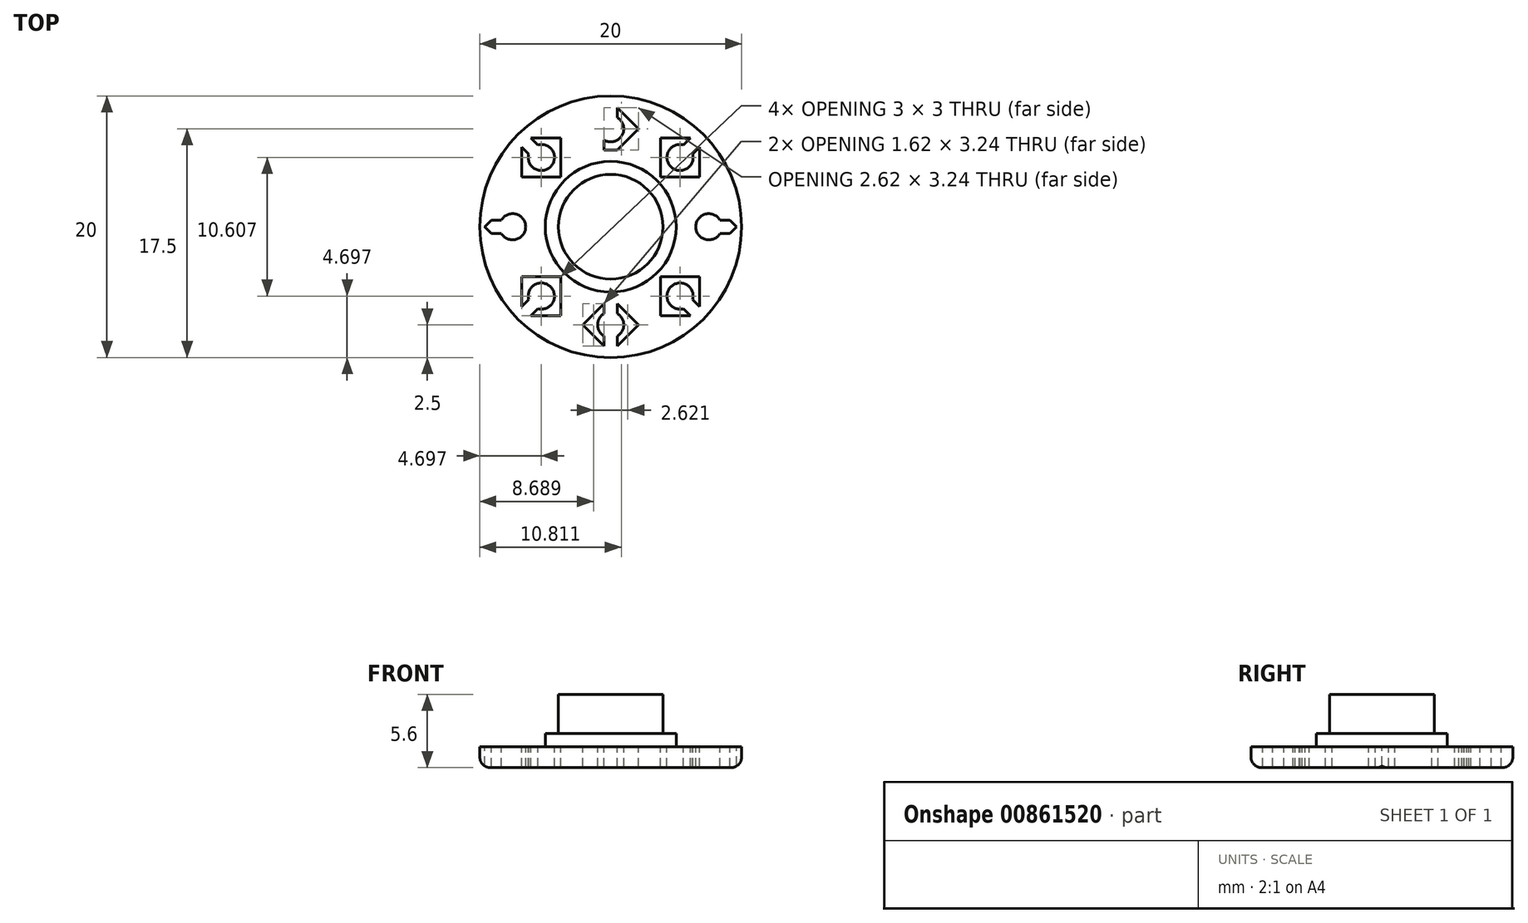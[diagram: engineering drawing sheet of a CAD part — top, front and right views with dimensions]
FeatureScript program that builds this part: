
annotation { "Feature Type Name" : "Feature", "Feature Type Description" : "" }
export const myFeature = defineFeature(function(context is Context, id is Id, definition is map)
    precondition{}
    {
        {
            var Q0;
            Q0=qCreatedBy(makeId("Top.planeOp"),FACE);
            var sketch = newSketch(context, id + "F0", { "sketchPlane" : qUnion([Q0])});
            skCircle(sketch, "E0", {"center": v(0, 0) * mm, "radius": 10 * mm});
            skSolve(sketch);
        }
        {
            var Q0;
            Q0=makeQuery(id+"F0.imprint","IMPRINT",FACE,{"disambiguationData":[TD([[makeQuery(id+"F0.imprint","IMPRINT",EDGE,{"derivedFrom":sQuery(id+"F0.wireOp",EDGE,"E0")}),1.0]])]});
            extrude(context, id + "F1", {"entities" : qUnion([Q0]), "depth" : 1.6 * mm, "offsetDistance" : 25 * mm});
        }
        {
            var Q0;
            Q0=makeQuery(id+"F1.opExtrude","CAP_FACE",FACE,{"disambiguationData":[OSD([sQuery(id+"F0.wireOp",EDGE,"E0")])],"isStart":false});
            var sketch = newSketch(context, id + "F2", { "sketchPlane" : qUnion([Q0])});
            skCircle(sketch, "E1", {"center": v(0, 0) * mm, "radius": 5 * mm});
            skSolve(sketch);
        }
        {
            var Q0;
            Q0=makeQuery(id+"F2.imprint","IMPRINT",FACE,{"disambiguationData":[TD([[makeQuery(id+"F2.imprint","IMPRINT",EDGE,{"derivedFrom":sQuery(id+"F2.wireOp",EDGE,"E1")}),1.0]])]});
            extrude(context, id + "F3", {"entities" : qUnion([Q0]), "operationType" : NewBodyOperationType.ADD, "depth" : 1 * mm, "offsetDistance" : 25 * mm});
        }
        {
            var Q0;
            Q0=makeQuery(id+"F3.opExtrude","CAP_FACE",FACE,{"disambiguationData":[OSD([sQuery(id+"F2.wireOp",EDGE,"E1")])],"isStart":false});
            var sketch = newSketch(context, id + "F4", { "sketchPlane" : qUnion([Q0])});
            skCircle(sketch, "E2", {"center": v(0, 0) * mm, "radius": 4 * mm});
            skSolve(sketch);
        }
        {
            var Q0;
            Q0=makeQuery(id+"F4.imprint","IMPRINT",FACE,{"disambiguationData":[TD([[makeQuery(id+"F4.imprint","IMPRINT",EDGE,{"derivedFrom":sQuery(id+"F4.wireOp",EDGE,"E2")}),1.0]])]});
            extrude(context, id + "F5", {"entities" : qUnion([Q0]), "depth" : 3 * mm, "offsetDistance" : 25 * mm});
        }
        {
            var Q0;
            Q0=makeQuery(id+"F1.opExtrude","CAP_FACE",FACE,{"disambiguationData":[OSD([sQuery(id+"F0.wireOp",EDGE,"E0")])],"isStart":false});
            var sketch = newSketch(context, id + "F6", { "sketchPlane" : qUnion([Q0])});
            skLineSegment(sketch, "E3", {"start": v(0, 5.38) * mm, "end": v(-2.12, 7.5) * mm});
            skLineSegment(sketch, "E4", {"start": v(-2.12, 7.5) * mm, "end": v(0, 9.62) * mm});
            skLineSegment(sketch, "E5", {"start": v(0, 5.38) * mm, "end": v(2.12, 7.5) * mm});
            skLineSegment(sketch, "E6", {"start": v(2.12, 7.5) * mm, "end": v(0, 9.62) * mm});
            skLineSegment(sketch, "E7", {"start": v(0, 5.38) * mm, "end": v(0, 5) * mm});
            skLineSegment(sketch, "E8", {"start": v(0, 9.62) * mm, "end": v(0, 10) * mm});
            skCircle(sketch, "E9", {"center": v(0, 7.5) * mm, "radius": 1 * mm});
            skCircle(sketch, "E10", {"center": v(0, 7.5) * mm, "radius": 2.12 * mm});
            skLineSegment(sketch, "E11", {"start": v(-0.5, 9.12) * mm, "end": v(0.5, 9.12) * mm});
            skLineSegment(sketch, "E12", {"start": v(0.5, 9.12) * mm, "end": v(0.5, 5.88) * mm});
            skLineSegment(sketch, "E13", {"start": v(0.5, 5.88) * mm, "end": v(-0.5, 5.88) * mm});
            skLineSegment(sketch, "E14", {"start": v(-0.5, 5.88) * mm, "end": v(-0.5, 9.12) * mm});
            skLineSegment(sketch, "E15.1.0", {"start": v(-6.8, 3.8) * mm, "end": v(-6.8, 6.8) * mm});
            skLineSegment(sketch, "E15.1.1", {"start": v(-3.8, 6.8) * mm, "end": v(-6.8, 6.8) * mm});
            skLineSegment(sketch, "E15.1.2", {"start": v(-3.8, 3.8) * mm, "end": v(-3.8, 6.8) * mm});
            skLineSegment(sketch, "E15.1.3", {"start": v(-3.8, 3.8) * mm, "end": v(-6.8, 3.8) * mm});
            skLineSegment(sketch, "E15.1.4", {"start": v(-4.51, 3.8) * mm, "end": v(-6.8, 6.1) * mm});
            skLineSegment(sketch, "E15.1.5", {"start": v(-6.1, 6.8) * mm, "end": v(-3.8, 4.51) * mm});
            skCircle(sketch, "E15.1.6", {"center": v(-5.3, 5.3) * mm, "radius": 1 * mm});
            skLineSegment(sketch, "E15.2.0", {"start": v(-7.5, -2.12) * mm, "end": v(-9.62, 0) * mm});
            skLineSegment(sketch, "E15.2.1", {"start": v(-7.5, 2.12) * mm, "end": v(-9.62, 0) * mm});
            skLineSegment(sketch, "E15.2.2", {"start": v(-5.38, 0) * mm, "end": v(-7.5, 2.12) * mm});
            skLineSegment(sketch, "E15.2.3", {"start": v(-5.38, 0) * mm, "end": v(-7.5, -2.12) * mm});
            skLineSegment(sketch, "E15.2.4", {"start": v(-5.88, -0.5) * mm, "end": v(-9.12, -0.5) * mm});
            skLineSegment(sketch, "E15.2.5", {"start": v(-9.12, 0.5) * mm, "end": v(-5.88, 0.5) * mm});
            skCircle(sketch, "E15.2.6", {"center": v(-7.5, 0) * mm, "radius": 1 * mm});
            skLineSegment(sketch, "E15.3.0", {"start": v(-3.8, -6.8) * mm, "end": v(-6.8, -6.8) * mm});
            skLineSegment(sketch, "E15.3.1", {"start": v(-6.8, -3.8) * mm, "end": v(-6.8, -6.8) * mm});
            skLineSegment(sketch, "E15.3.2", {"start": v(-3.8, -3.8) * mm, "end": v(-6.8, -3.8) * mm});
            skLineSegment(sketch, "E15.3.3", {"start": v(-3.8, -3.8) * mm, "end": v(-3.8, -6.8) * mm});
            skLineSegment(sketch, "E15.3.4", {"start": v(-3.8, -4.51) * mm, "end": v(-6.1, -6.8) * mm});
            skLineSegment(sketch, "E15.3.5", {"start": v(-6.8, -6.1) * mm, "end": v(-4.51, -3.8) * mm});
            skCircle(sketch, "E15.3.6", {"center": v(-5.3, -5.3) * mm, "radius": 1 * mm});
            skLineSegment(sketch, "E15.4.0", {"start": v(2.12, -7.5) * mm, "end": v(0, -9.62) * mm});
            skLineSegment(sketch, "E15.4.1", {"start": v(-2.12, -7.5) * mm, "end": v(0, -9.62) * mm});
            skLineSegment(sketch, "E15.4.2", {"start": v(0, -5.38) * mm, "end": v(-2.12, -7.5) * mm});
            skLineSegment(sketch, "E15.4.3", {"start": v(0, -5.38) * mm, "end": v(2.12, -7.5) * mm});
            skLineSegment(sketch, "E15.4.4", {"start": v(0.5, -5.88) * mm, "end": v(0.5, -9.12) * mm});
            skLineSegment(sketch, "E15.4.5", {"start": v(-0.5, -9.12) * mm, "end": v(-0.5, -5.88) * mm});
            skCircle(sketch, "E15.4.6", {"center": v(0, -7.5) * mm, "radius": 1 * mm});
            skLineSegment(sketch, "E15.5.0", {"start": v(6.8, -3.8) * mm, "end": v(6.8, -6.8) * mm});
            skLineSegment(sketch, "E15.5.1", {"start": v(3.8, -6.8) * mm, "end": v(6.8, -6.8) * mm});
            skLineSegment(sketch, "E15.5.2", {"start": v(3.8, -3.8) * mm, "end": v(3.8, -6.8) * mm});
            skLineSegment(sketch, "E15.5.3", {"start": v(3.8, -3.8) * mm, "end": v(6.8, -3.8) * mm});
            skLineSegment(sketch, "E15.5.4", {"start": v(4.51, -3.8) * mm, "end": v(6.8, -6.1) * mm});
            skLineSegment(sketch, "E15.5.5", {"start": v(6.1, -6.8) * mm, "end": v(3.8, -4.51) * mm});
            skCircle(sketch, "E15.5.6", {"center": v(5.3, -5.3) * mm, "radius": 1 * mm});
            skLineSegment(sketch, "E15.6.0", {"start": v(7.5, 2.12) * mm, "end": v(9.62, 0) * mm});
            skLineSegment(sketch, "E15.6.1", {"start": v(7.5, -2.12) * mm, "end": v(9.62, 0) * mm});
            skLineSegment(sketch, "E15.6.2", {"start": v(5.38, 0) * mm, "end": v(7.5, -2.12) * mm});
            skLineSegment(sketch, "E15.6.3", {"start": v(5.38, 0) * mm, "end": v(7.5, 2.12) * mm});
            skLineSegment(sketch, "E15.6.4", {"start": v(5.88, 0.5) * mm, "end": v(9.12, 0.5) * mm});
            skLineSegment(sketch, "E15.6.5", {"start": v(9.12, -0.5) * mm, "end": v(5.88, -0.5) * mm});
            skCircle(sketch, "E15.6.6", {"center": v(7.5, 0) * mm, "radius": 1 * mm});
            skLineSegment(sketch, "E15.7.0", {"start": v(3.8, 6.8) * mm, "end": v(6.8, 6.8) * mm});
            skLineSegment(sketch, "E15.7.1", {"start": v(6.8, 3.8) * mm, "end": v(6.8, 6.8) * mm});
            skLineSegment(sketch, "E15.7.2", {"start": v(3.8, 3.8) * mm, "end": v(6.8, 3.8) * mm});
            skLineSegment(sketch, "E15.7.3", {"start": v(3.8, 3.8) * mm, "end": v(3.8, 6.8) * mm});
            skLineSegment(sketch, "E15.7.4", {"start": v(3.8, 4.51) * mm, "end": v(6.1, 6.8) * mm});
            skLineSegment(sketch, "E15.7.5", {"start": v(6.8, 6.1) * mm, "end": v(4.51, 3.8) * mm});
            skCircle(sketch, "E15.7.6", {"center": v(5.3, 5.3) * mm, "radius": 1 * mm});
            skPoint(sketch, "E15.center", {"position": v(0, 0) * mm});
            skSolve(sketch);
        }
        {
            var Q0;
            Q0=makeQuery(id+"F1.opExtrude","CAP_EDGE",EDGE,{"disambiguationData":[OSD([sQuery(id+"F0.wireOp",EDGE,"E0")])],"isStart":true});
            fillet(context, id + "F7", {"entities" : qUnion([Q0]), "radius" : .8 * mm, "tangentPropagation" : true, "allowEdgeOverflow" : false});
        }
        {
            var Q0;
            {var subQ0=sQuery(id+"F6.wireOp",EDGE,"E14");var subQ3=sQuery(id+"F6.wireOp",EDGE,"E9");var subQ5=makeQuery(id+"F6.imprint","INTERSECT",VERTEX,{"disambiguationData":[OD(0.0)],"derivedFrom":[subQ3,subQ0]});Q0=makeQuery(id+"F6.imprint","IMPRINT",FACE,{"disambiguationData":[TD([[makeQuery(id+"F6.imprint","IMPRINT",EDGE,{"disambiguationData":[TD([[subQ5,-1.0]])],"derivedFrom":subQ3}),-1.0]])]});}
            var Q1;
            {var subQ0=sQuery(id+"F6.wireOp",EDGE,"E12");var subQ1=sQuery(id+"F6.wireOp",EDGE,"E9");var subQ2=makeQuery(id+"F6.imprint","INTERSECT",VERTEX,{"disambiguationData":[OD(0.0)],"derivedFrom":[subQ1,subQ0]});Q1=makeQuery(id+"F6.imprint","IMPRINT",FACE,{"disambiguationData":[TD([[makeQuery(id+"F6.imprint","IMPRINT",EDGE,{"disambiguationData":[TD([[subQ2,1.0]])],"derivedFrom":subQ1}),-1.0]])]});}
            var Q2;
            {var subQ1=sQuery(id+"F6.wireOp",EDGE,"E15.7.3");var subQ5=sQuery(id+"F6.wireOp",EDGE,"E15.7.0");var subQ6=makeQuery(id+"F6.imprint","INTERSECT",VERTEX,{"derivedFrom":[subQ5,subQ1]});Q2=makeQuery(id+"F6.imprint","IMPRINT",FACE,{"disambiguationData":[TD([[makeQuery(id+"F6.imprint","IMPRINT",EDGE,{"disambiguationData":[TD([[subQ6,-1.0]])],"derivedFrom":subQ5}),-1.0]])]});}
            var Q3;
            {var subQ1=sQuery(id+"F6.wireOp",EDGE,"E15.7.2");var subQ5=sQuery(id+"F6.wireOp",EDGE,"E15.7.1");var subQ6=makeQuery(id+"F6.imprint","INTERSECT",VERTEX,{"derivedFrom":[subQ5,subQ1]});Q3=makeQuery(id+"F6.imprint","IMPRINT",FACE,{"disambiguationData":[TD([[makeQuery(id+"F6.imprint","IMPRINT",EDGE,{"disambiguationData":[TD([[subQ6,-1.0]])],"derivedFrom":subQ5}),1.0]])]});}
            var Q4;
            {var subQ0=sQuery(id+"F6.wireOp",EDGE,"E15.6.6");var subQ1=sQuery(id+"F6.wireOp",EDGE,"E15.6.4");var subQ2=makeQuery(id+"F6.imprint","INTERSECT",VERTEX,{"disambiguationData":[OD(0.0)],"derivedFrom":[subQ1,subQ0]});Q4=makeQuery(id+"F6.imprint","IMPRINT",FACE,{"disambiguationData":[TD([[makeQuery(id+"F6.imprint","IMPRINT",EDGE,{"disambiguationData":[TD([[subQ2,-1.0]])],"derivedFrom":subQ1}),-1.0]])]});}
            var Q5;
            {var subQ1=sQuery(id+"F6.wireOp",EDGE,"E15.6.0");var subQ5=sQuery(id+"F6.wireOp",EDGE,"E15.6.1");var subQ6=makeQuery(id+"F6.imprint","INTERSECT",VERTEX,{"derivedFrom":[subQ1,subQ5]});Q5=makeQuery(id+"F6.imprint","IMPRINT",FACE,{"disambiguationData":[TD([[makeQuery(id+"F6.imprint","IMPRINT",EDGE,{"disambiguationData":[TD([[subQ6,1.0]])],"derivedFrom":subQ1}),-1.0]])]});}
            var Q6;
            {var subQ0=sQuery(id+"F6.wireOp",EDGE,"E15.6.6");var subQ1=sQuery(id+"F6.wireOp",EDGE,"E15.6.4");var subQ2=makeQuery(id+"F6.imprint","INTERSECT",VERTEX,{"disambiguationData":[OD(0.0)],"derivedFrom":[subQ1,subQ0]});Q6=makeQuery(id+"F6.imprint","IMPRINT",FACE,{"disambiguationData":[TD([[makeQuery(id+"F6.imprint","IMPRINT",EDGE,{"disambiguationData":[TD([[subQ2,-1.0]])],"derivedFrom":subQ1}),1.0]])]});}
            var Q7;
            {var subQ0=sQuery(id+"F6.wireOp",EDGE,"E15.6.6");var subQ1=sQuery(id+"F6.wireOp",EDGE,"E15.6.5");var subQ2=makeQuery(id+"F6.imprint","INTERSECT",VERTEX,{"disambiguationData":[OD(0.0)],"derivedFrom":[subQ1,subQ0]});Q7=makeQuery(id+"F6.imprint","IMPRINT",FACE,{"disambiguationData":[TD([[makeQuery(id+"F6.imprint","IMPRINT",EDGE,{"disambiguationData":[TD([[subQ2,-1.0]])],"derivedFrom":subQ1}),1.0]])]});}
            var Q8;
            {var subQ1=sQuery(id+"F6.wireOp",EDGE,"E15.2.0");var subQ5=sQuery(id+"F6.wireOp",EDGE,"E15.2.1");var subQ6=makeQuery(id+"F6.imprint","INTERSECT",VERTEX,{"derivedFrom":[subQ1,subQ5]});Q8=makeQuery(id+"F6.imprint","IMPRINT",FACE,{"disambiguationData":[TD([[makeQuery(id+"F6.imprint","IMPRINT",EDGE,{"disambiguationData":[TD([[subQ6,1.0]])],"derivedFrom":subQ1}),-1.0]])]});}
            var Q9;
            {var subQ0=sQuery(id+"F6.wireOp",EDGE,"E15.2.6");var subQ1=sQuery(id+"F6.wireOp",EDGE,"E15.2.5");var subQ2=makeQuery(id+"F6.imprint","INTERSECT",VERTEX,{"disambiguationData":[OD(0.0)],"derivedFrom":[subQ1,subQ0]});Q9=makeQuery(id+"F6.imprint","IMPRINT",FACE,{"disambiguationData":[TD([[makeQuery(id+"F6.imprint","IMPRINT",EDGE,{"disambiguationData":[TD([[subQ2,-1.0]])],"derivedFrom":subQ1}),1.0]])]});}
            var Q10;
            {var subQ0=sQuery(id+"F6.wireOp",EDGE,"E15.2.6");var subQ1=sQuery(id+"F6.wireOp",EDGE,"E15.2.4");var subQ2=makeQuery(id+"F6.imprint","INTERSECT",VERTEX,{"disambiguationData":[OD(0.0)],"derivedFrom":[subQ1,subQ0]});Q10=makeQuery(id+"F6.imprint","IMPRINT",FACE,{"disambiguationData":[TD([[makeQuery(id+"F6.imprint","IMPRINT",EDGE,{"disambiguationData":[TD([[subQ2,-1.0]])],"derivedFrom":subQ1}),-1.0]])]});}
            var Q11;
            {var subQ0=sQuery(id+"F6.wireOp",EDGE,"E15.2.6");var subQ1=sQuery(id+"F6.wireOp",EDGE,"E15.2.4");var subQ2=makeQuery(id+"F6.imprint","INTERSECT",VERTEX,{"disambiguationData":[OD(0.0)],"derivedFrom":[subQ1,subQ0]});Q11=makeQuery(id+"F6.imprint","IMPRINT",FACE,{"disambiguationData":[TD([[makeQuery(id+"F6.imprint","IMPRINT",EDGE,{"disambiguationData":[TD([[subQ2,-1.0]])],"derivedFrom":subQ1}),1.0]])]});}
            var Q12;
            {var subQ1=sQuery(id+"F6.wireOp",EDGE,"E15.4.2");var subQ5=sQuery(id+"F6.wireOp",EDGE,"E15.4.1");var subQ6=makeQuery(id+"F6.imprint","INTERSECT",VERTEX,{"derivedFrom":[subQ5,subQ1]});Q12=makeQuery(id+"F6.imprint","IMPRINT",FACE,{"disambiguationData":[TD([[makeQuery(id+"F6.imprint","IMPRINT",EDGE,{"disambiguationData":[TD([[subQ6,-1.0]])],"derivedFrom":subQ5}),1.0]])]});}
            var Q13;
            {var subQ1=sQuery(id+"F6.wireOp",EDGE,"E15.4.3");var subQ5=sQuery(id+"F6.wireOp",EDGE,"E15.4.0");var subQ6=makeQuery(id+"F6.imprint","INTERSECT",VERTEX,{"derivedFrom":[subQ5,subQ1]});Q13=makeQuery(id+"F6.imprint","IMPRINT",FACE,{"disambiguationData":[TD([[makeQuery(id+"F6.imprint","IMPRINT",EDGE,{"disambiguationData":[TD([[subQ6,-1.0]])],"derivedFrom":subQ5}),-1.0]])]});}
            var Q14;
            {var subQ1=sQuery(id+"F6.wireOp",EDGE,"E15.5.3");var subQ5=sQuery(id+"F6.wireOp",EDGE,"E15.5.0");var subQ6=makeQuery(id+"F6.imprint","INTERSECT",VERTEX,{"derivedFrom":[subQ5,subQ1]});Q14=makeQuery(id+"F6.imprint","IMPRINT",FACE,{"disambiguationData":[TD([[makeQuery(id+"F6.imprint","IMPRINT",EDGE,{"disambiguationData":[TD([[subQ6,-1.0]])],"derivedFrom":subQ5}),-1.0]])]});}
            var Q15;
            {var subQ1=sQuery(id+"F6.wireOp",EDGE,"E15.5.2");var subQ6=sQuery(id+"F6.wireOp",EDGE,"E15.5.3");var subQ9=makeQuery(id+"F6.imprint","INTERSECT",VERTEX,{"derivedFrom":[subQ1,subQ6]});Q15=makeQuery(id+"F6.imprint","IMPRINT",FACE,{"disambiguationData":[TD([[makeQuery(id+"F6.imprint","IMPRINT",EDGE,{"disambiguationData":[TD([[subQ9,-1.0]])],"derivedFrom":subQ1}),1.0]])]});}
            var Q16;
            {var subQ1=sQuery(id+"F6.wireOp",EDGE,"E15.5.2");var subQ5=sQuery(id+"F6.wireOp",EDGE,"E15.5.1");var subQ6=makeQuery(id+"F6.imprint","INTERSECT",VERTEX,{"derivedFrom":[subQ5,subQ1]});Q16=makeQuery(id+"F6.imprint","IMPRINT",FACE,{"disambiguationData":[TD([[makeQuery(id+"F6.imprint","IMPRINT",EDGE,{"disambiguationData":[TD([[subQ6,-1.0]])],"derivedFrom":subQ5}),1.0]])]});}
            var Q17;
            {var subQ1=sQuery(id+"F6.wireOp",EDGE,"E15.3.2");var subQ5=sQuery(id+"F6.wireOp",EDGE,"E15.3.1");var subQ6=makeQuery(id+"F6.imprint","INTERSECT",VERTEX,{"derivedFrom":[subQ5,subQ1]});Q17=makeQuery(id+"F6.imprint","IMPRINT",FACE,{"disambiguationData":[TD([[makeQuery(id+"F6.imprint","IMPRINT",EDGE,{"disambiguationData":[TD([[subQ6,-1.0]])],"derivedFrom":subQ5}),1.0]])]});}
            var Q18;
            {var subQ1=sQuery(id+"F6.wireOp",EDGE,"E15.3.2");var subQ6=sQuery(id+"F6.wireOp",EDGE,"E15.3.3");var subQ9=makeQuery(id+"F6.imprint","INTERSECT",VERTEX,{"derivedFrom":[subQ1,subQ6]});Q18=makeQuery(id+"F6.imprint","IMPRINT",FACE,{"disambiguationData":[TD([[makeQuery(id+"F6.imprint","IMPRINT",EDGE,{"disambiguationData":[TD([[subQ9,-1.0]])],"derivedFrom":subQ1}),1.0]])]});}
            var Q19;
            {var subQ1=sQuery(id+"F6.wireOp",EDGE,"E15.3.3");var subQ5=sQuery(id+"F6.wireOp",EDGE,"E15.3.0");var subQ6=makeQuery(id+"F6.imprint","INTERSECT",VERTEX,{"derivedFrom":[subQ5,subQ1]});Q19=makeQuery(id+"F6.imprint","IMPRINT",FACE,{"disambiguationData":[TD([[makeQuery(id+"F6.imprint","IMPRINT",EDGE,{"disambiguationData":[TD([[subQ6,-1.0]])],"derivedFrom":subQ5}),-1.0]])]});}
            var Q20;
            {var subQ1=sQuery(id+"F6.wireOp",EDGE,"E15.7.2");var subQ6=sQuery(id+"F6.wireOp",EDGE,"E15.7.3");var subQ9=makeQuery(id+"F6.imprint","INTERSECT",VERTEX,{"derivedFrom":[subQ1,subQ6]});Q20=makeQuery(id+"F6.imprint","IMPRINT",FACE,{"disambiguationData":[TD([[makeQuery(id+"F6.imprint","IMPRINT",EDGE,{"disambiguationData":[TD([[subQ9,-1.0]])],"derivedFrom":subQ1}),1.0]])]});}
            var Q21;
            {var subQ1=sQuery(id+"F6.wireOp",EDGE,"E15.1.3");var subQ5=sQuery(id+"F6.wireOp",EDGE,"E15.1.0");var subQ6=makeQuery(id+"F6.imprint","INTERSECT",VERTEX,{"derivedFrom":[subQ5,subQ1]});Q21=makeQuery(id+"F6.imprint","IMPRINT",FACE,{"disambiguationData":[TD([[makeQuery(id+"F6.imprint","IMPRINT",EDGE,{"disambiguationData":[TD([[subQ6,-1.0]])],"derivedFrom":subQ5}),-1.0]])]});}
            var Q22;
            {var subQ1=sQuery(id+"F6.wireOp",EDGE,"E15.1.2");var subQ6=sQuery(id+"F6.wireOp",EDGE,"E15.1.3");var subQ9=makeQuery(id+"F6.imprint","INTERSECT",VERTEX,{"derivedFrom":[subQ1,subQ6]});Q22=makeQuery(id+"F6.imprint","IMPRINT",FACE,{"disambiguationData":[TD([[makeQuery(id+"F6.imprint","IMPRINT",EDGE,{"disambiguationData":[TD([[subQ9,-1.0]])],"derivedFrom":subQ1}),1.0]])]});}
            var Q23;
            {var subQ1=sQuery(id+"F6.wireOp",EDGE,"E15.1.2");var subQ5=sQuery(id+"F6.wireOp",EDGE,"E15.1.1");var subQ6=makeQuery(id+"F6.imprint","INTERSECT",VERTEX,{"derivedFrom":[subQ5,subQ1]});Q23=makeQuery(id+"F6.imprint","IMPRINT",FACE,{"disambiguationData":[TD([[makeQuery(id+"F6.imprint","IMPRINT",EDGE,{"disambiguationData":[TD([[subQ6,-1.0]])],"derivedFrom":subQ5}),1.0]])]});}
            extrude(context, id + "F8", {"entities" : qUnion([Q0, Q1, Q2, Q3, Q4, Q5, Q6, Q7, Q8, Q9, Q10, Q11, Q12, Q13, Q14, Q15, Q16, Q17, Q18, Q19, Q20, Q21, Q22, Q23]), "operationType" : NewBodyOperationType.REMOVE, "oppositeDirection" : true, "depth" : 25 * mm, "offsetDistance" : 25 * mm});
        }
    });
